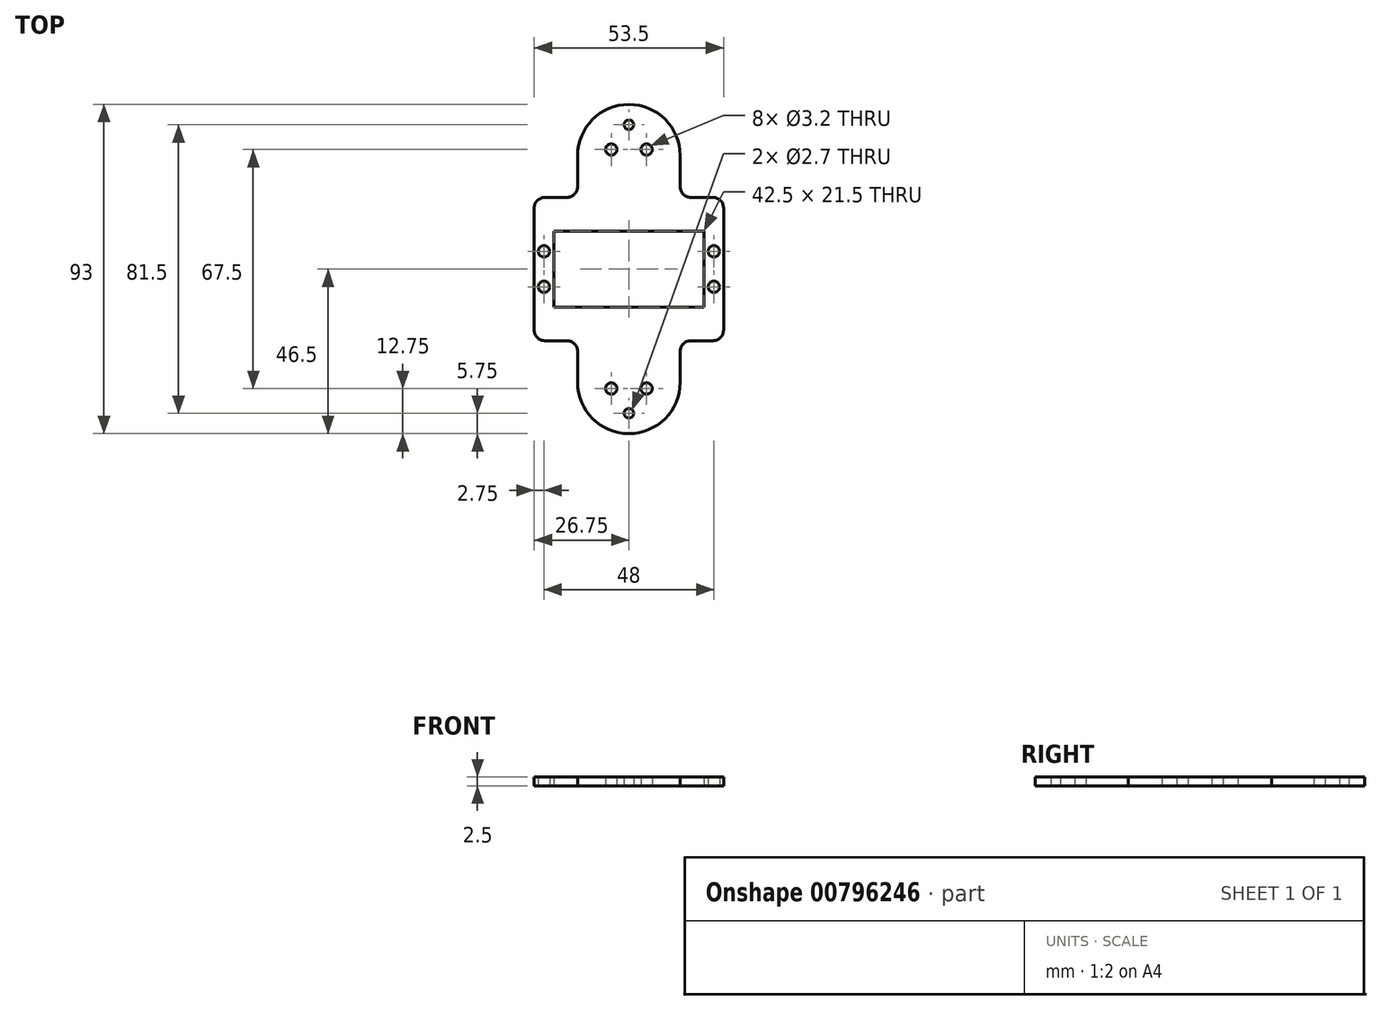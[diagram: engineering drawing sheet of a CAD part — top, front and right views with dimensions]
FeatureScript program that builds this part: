
annotation { "Feature Type Name" : "Feature", "Feature Type Description" : "" }
export const myFeature = defineFeature(function(context is Context, id is Id, definition is map)
    precondition{}
    {
        {
            var Q0;
            Q0=qCreatedBy(makeId("Top.planeOp"),FACE);
            var sketch = newSketch(context, id + "F0", { "sketchPlane" : qUnion([Q0])});
            skLineSegment(sketch, "E0", {"start": v(0, 0) * mm, "end": v(53.5, 0) * mm});
            skLineSegment(sketch, "E1", {"start": v(0, 0) * mm, "end": v(0, 17.25) * mm});
            skLineSegment(sketch, "E2", {"start": v(3, 20.25) * mm, "end": v(9.25, 20.25) * mm});
            skLineSegment(sketch, "E3", {"start": v(12.25, 23.25) * mm, "end": v(12.25, 32) * mm});
            skLineSegment(sketch, "E4", {"start": v(26.75, -60.43) * mm, "end": v(26.75, 61.52) * mm});
            skLineSegment(sketch, "E5", {"start": v(12.25, 32) * mm, "end": v(26.75, 32) * mm});
            skLineSegment(sketch, "E6.MirrorCS", {"start": v(53.5, 0) * mm, "end": v(53.5, 17.25) * mm});
            skLineSegment(sketch, "E7.MirrorCS", {"start": v(50.5, 20.25) * mm, "end": v(44.25, 20.25) * mm});
            skLineSegment(sketch, "E8.MirrorCS", {"start": v(41.25, 23.25) * mm, "end": v(41.25, 32) * mm});
            skLineSegment(sketch, "E9.MirrorCS", {"start": v(41.25, 32) * mm, "end": v(26.75, 32) * mm});
            skLineSegment(sketch, "E10.MirrorCS", {"start": v(0, 0) * mm, "end": v(0, -17.25) * mm});
            skLineSegment(sketch, "E11.MirrorCS", {"start": v(3, -20.25) * mm, "end": v(9.25, -20.25) * mm});
            skLineSegment(sketch, "E12.MirrorCS", {"start": v(12.25, -23.25) * mm, "end": v(12.25, -32) * mm});
            skLineSegment(sketch, "E13.MirrorCS", {"start": v(12.25, -32) * mm, "end": v(26.75, -32) * mm});
            skLineSegment(sketch, "E14.MirrorCS", {"start": v(41.25, -32) * mm, "end": v(26.75, -32) * mm});
            skLineSegment(sketch, "E15.MirrorCS", {"start": v(50.5, -20.25) * mm, "end": v(44.25, -20.25) * mm});
            skLineSegment(sketch, "E16.MirrorCS", {"start": v(53.5, 0) * mm, "end": v(53.5, -17.25) * mm});
            skLineSegment(sketch, "E17.MirrorCS", {"start": v(41.25, -23.25) * mm, "end": v(41.25, -32) * mm});
            skLineSegment(sketch, "E18", {"start": v(5.5, 0) * mm, "end": v(5.5, 10.75) * mm});
            skLineSegment(sketch, "E19", {"start": v(5.5, 10.75) * mm, "end": v(26.75, 10.75) * mm});
            skLineSegment(sketch, "E20.MirrorCS", {"start": v(48, 10.75) * mm, "end": v(26.75, 10.75) * mm});
            skLineSegment(sketch, "E21.MirrorCS", {"start": v(48, 0) * mm, "end": v(48, 10.75) * mm});
            skLineSegment(sketch, "E22.MirrorCS", {"start": v(5.5, 0) * mm, "end": v(5.5, -10.75) * mm});
            skLineSegment(sketch, "E23.MirrorCS", {"start": v(5.5, -10.75) * mm, "end": v(26.75, -10.75) * mm});
            skLineSegment(sketch, "E24.MirrorCS", {"start": v(48, -10.75) * mm, "end": v(26.75, -10.75) * mm});
            skLineSegment(sketch, "E25.MirrorCS", {"start": v(48, 0) * mm, "end": v(48, -10.75) * mm});
            skArc(sketch, "E26", {"start": v(41.25, 32) * mm, "mid": v(26.75, 46.5) * mm, "end": v(12.25, 32) * mm});
            skArc(sketch, "E27.MirrorCS", {"start": v(41.25, -32) * mm, "mid": v(26.75, -46.5) * mm, "end": v(12.25, -32) * mm});
            skCircle(sketch, "E28", {"center": v(2.75, 5) * mm, "radius": 1.6 * mm});
            skCircle(sketch, "E29.MirrorC", {"center": v(50.75, 5) * mm, "radius": 1.6 * mm});
            skCircle(sketch, "E30.MirrorC", {"center": v(2.75, -5) * mm, "radius": 1.6 * mm});
            skCircle(sketch, "E31.MirrorC", {"center": v(50.75, -5) * mm, "radius": 1.6 * mm});
            skCircle(sketch, "E32", {"center": v(21.75, 33.75) * mm, "radius": 1.6 * mm});
            skCircle(sketch, "E33.MirrorC", {"center": v(21.75, -33.75) * mm, "radius": 1.6 * mm});
            skCircle(sketch, "E34.MirrorC", {"center": v(31.75, 33.75) * mm, "radius": 1.6 * mm});
            skCircle(sketch, "E35.MirrorC", {"center": v(31.75, -33.75) * mm, "radius": 1.6 * mm});
            skCircle(sketch, "E36", {"center": v(26.75, 40.75) * mm, "radius": 1.35 * mm});
            skCircle(sketch, "E37.MirrorC", {"center": v(26.75, -40.75) * mm, "radius": 1.35 * mm});
            skPoint(sketch, "E38.visualSharp", {"position": v(0, -20.25) * mm});
            skArc(sketch, "E38.filletArc", {"start": v(0, -17.25) * mm, "mid": v(0.88, -19.37) * mm, "end": v(3, -20.25) * mm});
            skPoint(sketch, "E39.visualSharp", {"position": v(0, 20.25) * mm});
            skArc(sketch, "E39.filletArc", {"start": v(3, 20.25) * mm, "mid": v(0.88, 19.37) * mm, "end": v(0, 17.25) * mm});
            skPoint(sketch, "E40.visualSharp", {"position": v(12.25, 20.25) * mm});
            skArc(sketch, "E40.filletArc", {"start": v(9.25, 20.25) * mm, "mid": v(11.37, 21.13) * mm, "end": v(12.25, 23.25) * mm});
            skPoint(sketch, "E41.visualSharp", {"position": v(41.25, 20.25) * mm});
            skArc(sketch, "E41.filletArc", {"start": v(41.25, 23.25) * mm, "mid": v(42.13, 21.13) * mm, "end": v(44.25, 20.25) * mm});
            skPoint(sketch, "E42.visualSharp", {"position": v(53.5, 20.25) * mm});
            skArc(sketch, "E42.filletArc", {"start": v(53.5, 17.25) * mm, "mid": v(52.62, 19.37) * mm, "end": v(50.5, 20.25) * mm});
            skPoint(sketch, "E43.visualSharp", {"position": v(53.5, -20.25) * mm});
            skArc(sketch, "E43.filletArc", {"start": v(50.5, -20.25) * mm, "mid": v(52.62, -19.37) * mm, "end": v(53.5, -17.25) * mm});
            skPoint(sketch, "E44.visualSharp", {"position": v(41.25, -20.25) * mm});
            skArc(sketch, "E44.filletArc", {"start": v(44.25, -20.25) * mm, "mid": v(42.13, -21.13) * mm, "end": v(41.25, -23.25) * mm});
            skPoint(sketch, "E45.visualSharp", {"position": v(12.25, -20.25) * mm});
            skArc(sketch, "E45.filletArc", {"start": v(12.25, -23.25) * mm, "mid": v(11.37, -21.13) * mm, "end": v(9.25, -20.25) * mm});
            skSolve(sketch);
        }
        {
            var Q0;
            Q0 = qSketchRegion(id + "F0", true);
            extrude(context, id + "F1", {"entities" : qUnion([Q0]), "depth" : 2.5 * mm, "offsetDistance" : 25 * mm});
        }
    });
